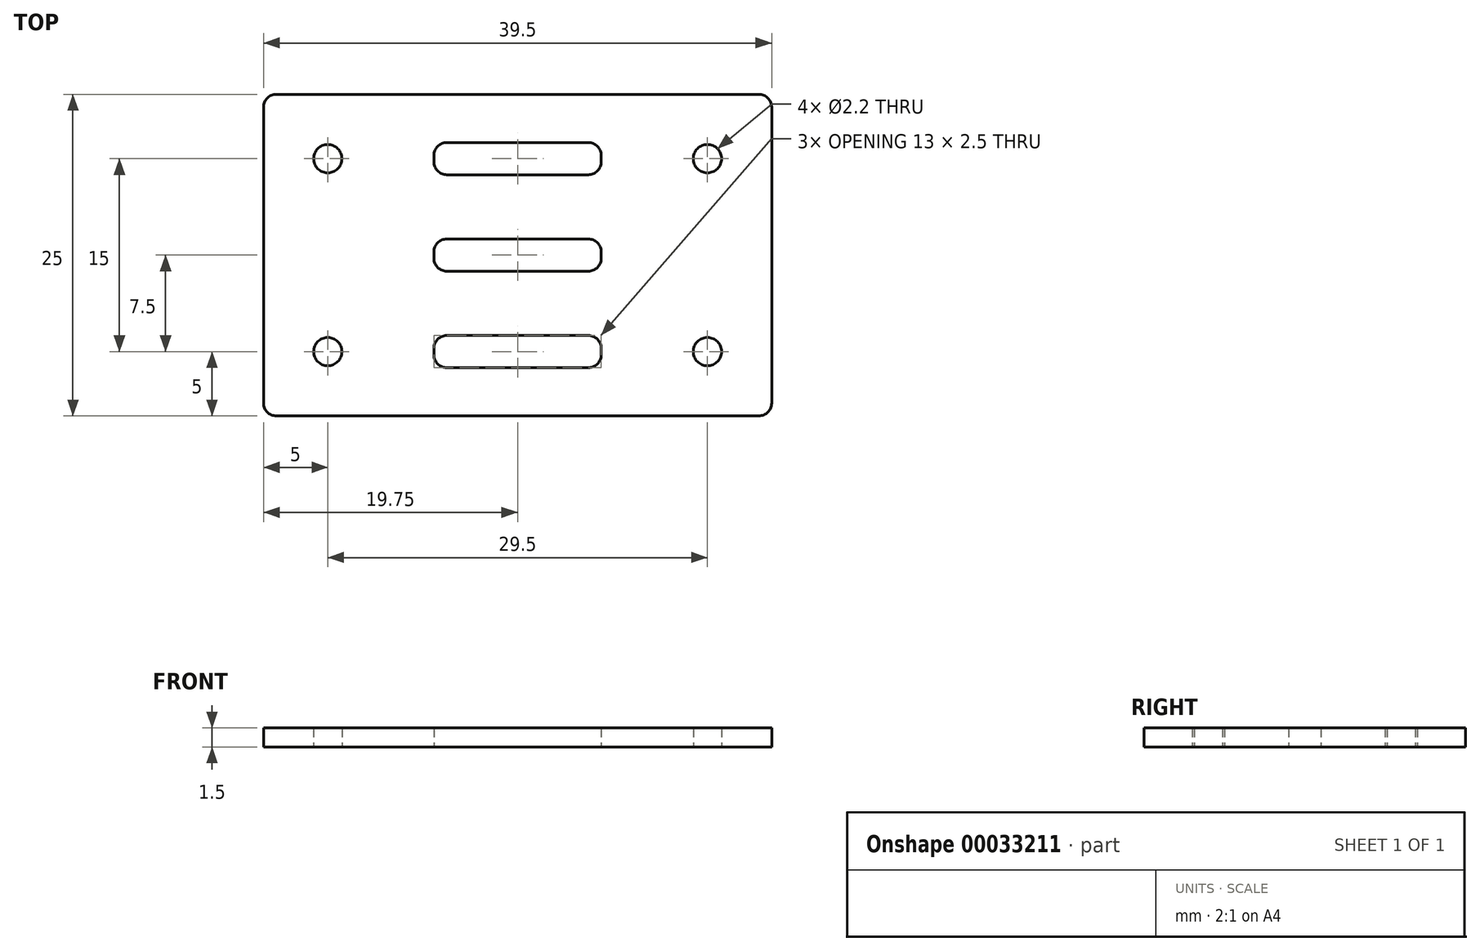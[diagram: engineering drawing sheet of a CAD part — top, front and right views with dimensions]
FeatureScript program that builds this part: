
annotation { "Feature Type Name" : "Feature", "Feature Type Description" : "" }
export const myFeature = defineFeature(function(context is Context, id is Id, definition is map)
    precondition{}
    {
        {
            var Q0;
            Q0=qCreatedBy(makeId("Top.planeOp"),FACE);
            var sketch = newSketch(context, id + "F0", { "sketchPlane" : qUnion([Q0])});
            skLineSegment(sketch, "E0.bottom", {"start": v(18.75, 12.5) * mm, "end": v(-18.75, 12.5) * mm});
            skLineSegment(sketch, "E0.top", {"start": v(18.75, -12.5) * mm, "end": v(-18.75, -12.5) * mm});
            skLineSegment(sketch, "E0.left", {"start": v(19.75, 11.5) * mm, "end": v(19.75, -11.5) * mm});
            skLineSegment(sketch, "E0.right", {"start": v(-19.75, 11.5) * mm, "end": v(-19.75, -11.5) * mm});
            skPoint(sketch, "E0.middle", {"position": v(0, 0) * mm});
            skCircle(sketch, "E1", {"center": v(14.75, 7.5) * mm, "radius": 1.1 * mm});
            skCircle(sketch, "E2.MirrorC", {"center": v(14.75, -7.5) * mm, "radius": 1.1 * mm});
            skCircle(sketch, "E3.MirrorC", {"center": v(-14.75, 7.5) * mm, "radius": 1.1 * mm});
            skLineSegment(sketch, "E4.bottom", {"start": v(-5.5, 8.75) * mm, "end": v(5.5, 8.75) * mm});
            skLineSegment(sketch, "E4.top", {"start": v(-5.5, 6.25) * mm, "end": v(5.5, 6.25) * mm});
            skLineSegment(sketch, "E4.left", {"start": v(-6.5, 7.75) * mm, "end": v(-6.5, 7.25) * mm});
            skLineSegment(sketch, "E4.right", {"start": v(6.5, 7.75) * mm, "end": v(6.5, 7.25) * mm});
            skPoint(sketch, "E4.middle", {"position": v(0, 7.5) * mm});
            skPoint(sketch, "E5.visualSharp", {"position": v(-6.5, 8.75) * mm});
            skArc(sketch, "E5.filletArc", {"start": v(-5.5, 8.75) * mm, "mid": v(-6.2, 8.46) * mm, "end": v(-6.5, 7.75) * mm});
            skPoint(sketch, "E6.visualSharp", {"position": v(-6.5, 6.25) * mm});
            skArc(sketch, "E6.filletArc", {"start": v(-6.5, 7.25) * mm, "mid": v(-6.2, 6.54) * mm, "end": v(-5.5, 6.25) * mm});
            skPoint(sketch, "E7.visualSharp", {"position": v(6.5, 8.75) * mm});
            skArc(sketch, "E7.filletArc", {"start": v(6.5, 7.75) * mm, "mid": v(6.2, 8.46) * mm, "end": v(5.5, 8.75) * mm});
            skPoint(sketch, "E8.visualSharp", {"position": v(6.5, 6.25) * mm});
            skArc(sketch, "E8.filletArc", {"start": v(5.5, 6.25) * mm, "mid": v(6.2, 6.54) * mm, "end": v(6.5, 7.25) * mm});
            skLineSegment(sketch, "E9.MirrorCS", {"start": v(-6.5, -7.75) * mm, "end": v(-6.5, -7.25) * mm});
            skLineSegment(sketch, "E10.MirrorCS", {"start": v(6.5, -7.75) * mm, "end": v(6.5, -7.25) * mm});
            skArc(sketch, "E11.MirrorCS", {"start": v(6.5, -7.75) * mm, "mid": v(6.2, -8.46) * mm, "end": v(5.5, -8.75) * mm});
            skArc(sketch, "E12.MirrorCS", {"start": v(-6.5, -7.25) * mm, "mid": v(-6.2, -6.54) * mm, "end": v(-5.5, -6.25) * mm});
            skPoint(sketch, "E13.MirrorP", {"position": v(6.5, -6.25) * mm});
            skPoint(sketch, "E14.MirrorP", {"position": v(6.5, -8.75) * mm});
            skArc(sketch, "E15.MirrorCS", {"start": v(-5.5, -8.75) * mm, "mid": v(-6.2, -8.46) * mm, "end": v(-6.5, -7.75) * mm});
            skArc(sketch, "E16.MirrorCS", {"start": v(5.5, -6.25) * mm, "mid": v(6.2, -6.54) * mm, "end": v(6.5, -7.25) * mm});
            skPoint(sketch, "E17.MirrorP", {"position": v(-6.5, -6.25) * mm});
            skLineSegment(sketch, "E18.MirrorCS", {"start": v(-5.5, -8.75) * mm, "end": v(5.5, -8.75) * mm});
            skPoint(sketch, "E19.MirrorP", {"position": v(0, -7.5) * mm});
            skLineSegment(sketch, "E20.MirrorCS", {"start": v(-5.5, -6.25) * mm, "end": v(5.5, -6.25) * mm});
            skPoint(sketch, "E21.MirrorP", {"position": v(-6.5, -8.75) * mm});
            skCircle(sketch, "E22.MirrorC", {"center": v(-14.75, -7.5) * mm, "radius": 1.1 * mm});
            skPoint(sketch, "E23.visualSharp", {"position": v(-19.75, 12.5) * mm});
            skArc(sketch, "E23.filletArc", {"start": v(-18.75, 12.5) * mm, "mid": v(-19.46, 12.2) * mm, "end": v(-19.75, 11.5) * mm});
            skPoint(sketch, "E24.visualSharp", {"position": v(-19.75, -12.5) * mm});
            skArc(sketch, "E24.filletArc", {"start": v(-19.75, -11.5) * mm, "mid": v(-19.46, -12.2) * mm, "end": v(-18.75, -12.5) * mm});
            skPoint(sketch, "E25.visualSharp", {"position": v(19.75, -12.5) * mm});
            skArc(sketch, "E25.filletArc", {"start": v(18.75, -12.5) * mm, "mid": v(19.46, -12.2) * mm, "end": v(19.75, -11.5) * mm});
            skPoint(sketch, "E26.visualSharp", {"position": v(19.75, 12.5) * mm});
            skArc(sketch, "E26.filletArc", {"start": v(19.75, 11.5) * mm, "mid": v(19.46, 12.2) * mm, "end": v(18.75, 12.5) * mm});
            skLineSegment(sketch, "E27.1.0.1", {"start": v(-5.5, 1.25) * mm, "end": v(5.5, 1.25) * mm});
            skLineSegment(sketch, "E27.1.0.2", {"start": v(-5.5, -1.25) * mm, "end": v(5.5, -1.25) * mm});
            skPoint(sketch, "E27.1.0.3", {"position": v(6.5, -1.25) * mm});
            skPoint(sketch, "E27.1.0.4", {"position": v(-6.5, -1.25) * mm});
            skPoint(sketch, "E27.1.0.5", {"position": v(-6.5, 1.25) * mm});
            skPoint(sketch, "E27.1.0.6", {"position": v(6.5, 1.25) * mm});
            skArc(sketch, "E27.1.0.7", {"start": v(5.5, -1.25) * mm, "mid": v(6.2, -0.96) * mm, "end": v(6.5, -0.25) * mm});
            skArc(sketch, "E27.1.0.8", {"start": v(-6.5, -0.25) * mm, "mid": v(-6.2, -0.96) * mm, "end": v(-5.5, -1.25) * mm});
            skArc(sketch, "E27.1.0.9", {"start": v(6.5, 0.25) * mm, "mid": v(6.2, 0.96) * mm, "end": v(5.5, 1.25) * mm});
            skArc(sketch, "E27.1.0.10", {"start": v(-5.5, 1.25) * mm, "mid": v(-6.2, 0.96) * mm, "end": v(-6.5, 0.25) * mm});
            skLineSegment(sketch, "E27.1.0.11", {"start": v(-6.5, 0.25) * mm, "end": v(-6.5, -0.25) * mm});
            skLineSegment(sketch, "E27.1.0.12", {"start": v(6.5, 0.25) * mm, "end": v(6.5, -0.25) * mm});
            skLineSegment(sketch, "E27.direction1", {"start": v(0, 7.5) * mm, "end": v(0, 0) * mm, "construction": true});
            skSolve(sketch);
        }
        {
            var Q0;
            Q0=qSketchRegion(id+"F0",true);
            extrude(context, id + "F1", {"entities" : qUnion([Q0]), "depth" : 1.5 * mm});
        }
    });
